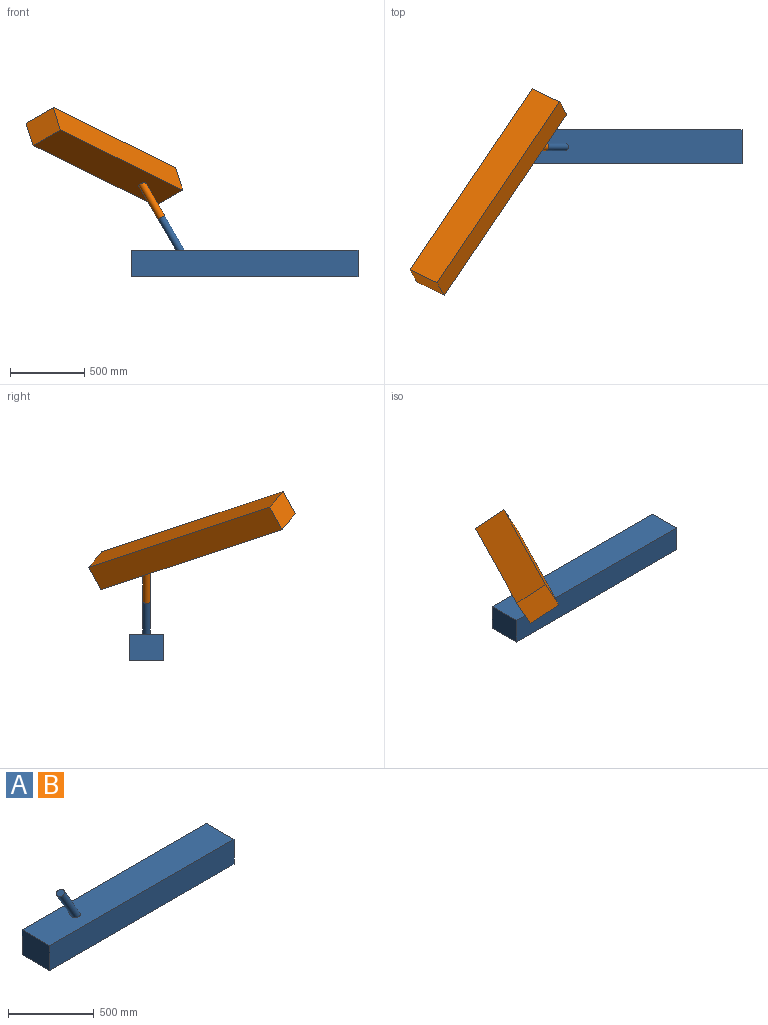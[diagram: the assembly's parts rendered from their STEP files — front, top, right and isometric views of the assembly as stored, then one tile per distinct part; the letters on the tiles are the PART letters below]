
ASSEMBLY  parts=2 mates=1
PART A: 8 faces, bbox 1530.2x234.8x415.7 mm
  f0: plane 228.6x177.8mm, normal (1,0,0), area 40645.1mm2, adj f1,f3,f4,f5
  f1: plane 1524x177.8mm, normal (0,1,0), area 270967.2mm2, adj f0,f2,f4,f5
  f2: plane 228.6x177.8mm, normal (-1,0,0), area 40645.1mm2, adj f1,f3,f4,f5
  f3: plane 1524x177.8mm, normal (0,-1,0), area 270967.2mm2, adj f0,f2,f4,f5
  f4: plane 1530.17x234.77mm, normal (0,0,1), area 346046mm2, adj f0,f1,f2,f3,f6
  f5: plane 1524x228.6mm, normal (0,0,-1), area 348386.4mm2, adj f0,f1,f2,f3
  f6: cylinder r=25.4mm len=257.16mm, axis (0.5,0,-0.87), area 40368.6mm2, adj f4,f7
  f7: plane 50.8x43.99mm, normal (-0.5,0,0.87), area 2026.8mm2, adj f6
PART B: same geometry as A
PLACE A t=(69.82,86.78,256.31)mm fixed
PLACE B rot(axis=(-0.48,0.83,-0.28),180deg) t=(-872.58,-217.49,973.38)mm
MATE revolute B.f6 <-> A.f6  axis (0.5,0,-0.87) through (-488.98,86.78,564.27)mm
